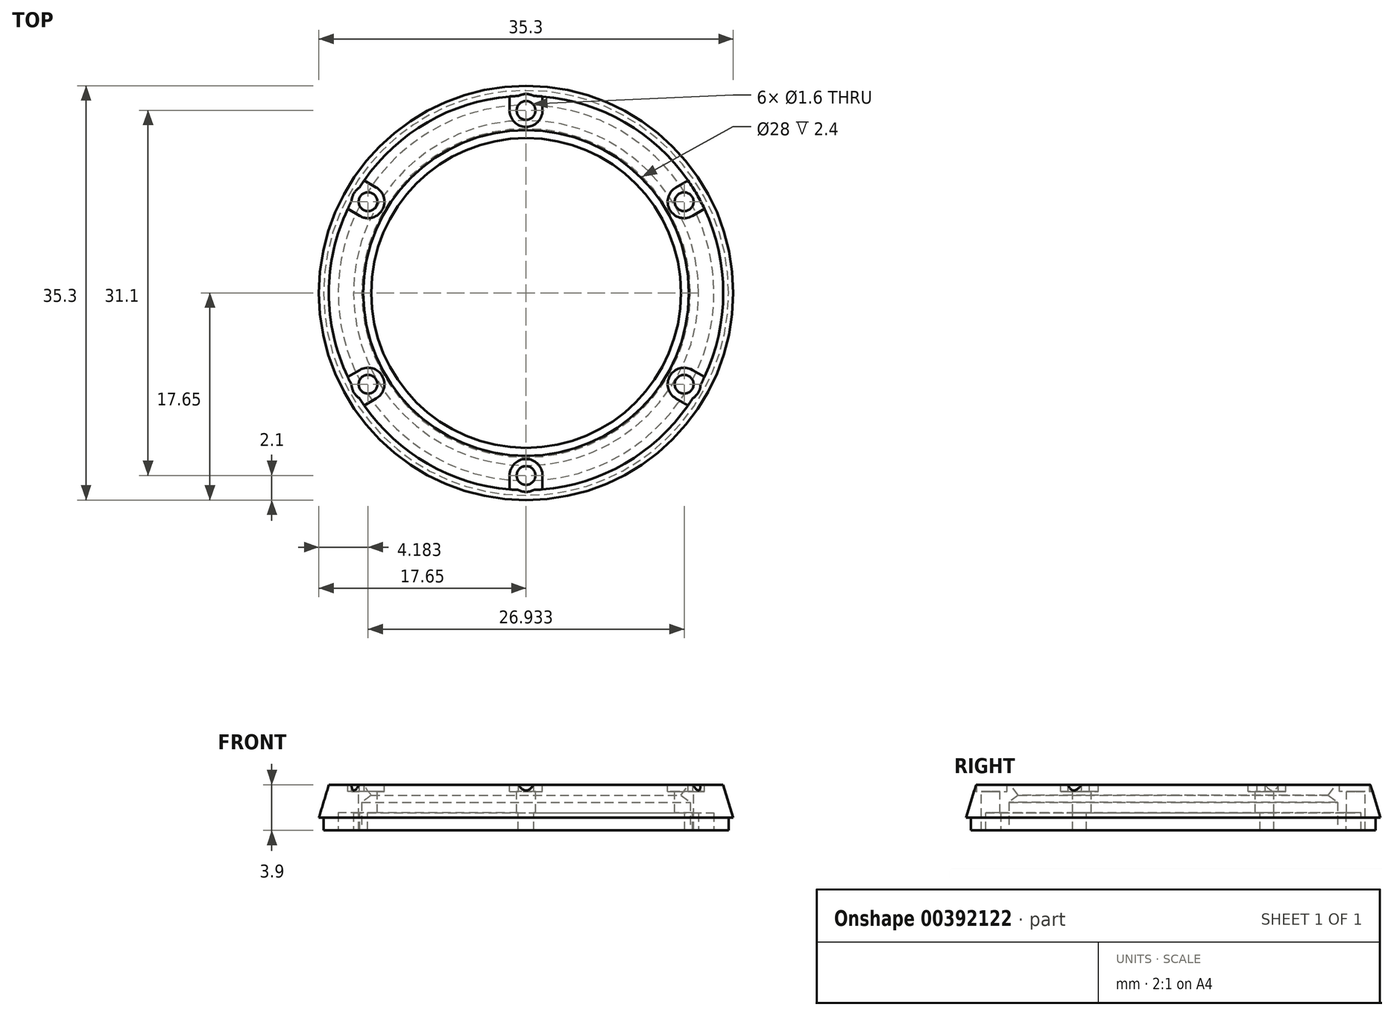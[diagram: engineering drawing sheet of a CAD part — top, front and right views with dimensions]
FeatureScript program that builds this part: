
annotation { "Feature Type Name" : "Feature", "Feature Type Description" : "" }
export const myFeature = defineFeature(function(context is Context, id is Id, definition is map)
    precondition{}
    {
        {
            var Q0;
            Q0=qCreatedBy(makeId("Front.planeOp"),FACE);
            var sketch = newSketch(context, id + "F0", { "sketchPlane" : qUnion([Q0])});
            skLineSegment(sketch, "E0", {"start": v(0, 0) * mm, "end": v(0, 11.47) * mm, "construction": true});
            skLineSegment(sketch, "E1", {"start": v(0, 0) * mm, "end": v(-14, 0) * mm, "construction": true});
            skLineSegment(sketch, "E2", {"start": v(-14, 0) * mm, "end": v(-14, 2.4) * mm});
            skLineSegment(sketch, "E3", {"start": v(-14, 2.4) * mm, "end": v(-13.2, 3) * mm});
            skLineSegment(sketch, "E4", {"start": v(-13.2, 3) * mm, "end": v(-13.88, 3.9) * mm});
            skLineSegment(sketch, "E5", {"start": v(-13.88, 3.9) * mm, "end": v(-16.8, 3.9) * mm});
            skLineSegment(sketch, "E6", {"start": v(-16.8, 3.9) * mm, "end": v(-17.65, 1.1) * mm});
            skLineSegment(sketch, "E7", {"start": v(-17.65, 1.1) * mm, "end": v(-17.25, 1.1) * mm});
            skLineSegment(sketch, "E8", {"start": v(-17.25, 1.1) * mm, "end": v(-17.25, 0) * mm});
            skLineSegment(sketch, "E9", {"start": v(-17.25, 0) * mm, "end": v(-14, 0) * mm});
            skLineSegment(sketch, "E10", {"start": v(-14.7, 0) * mm, "end": v(-14.7, 1.5) * mm});
            skLineSegment(sketch, "E11", {"start": v(-14.7, 1.5) * mm, "end": v(-16, 1.5) * mm});
            skLineSegment(sketch, "E12", {"start": v(-16, 1.5) * mm, "end": v(-16, 0) * mm});
            skSolve(sketch);
        }
        {
            var Q0;
            Q0=makeQuery(id+"F0.imprint","IMPRINT",FACE,{"disambiguationData":[TD([[makeQuery(id+"F0.imprint","IMPRINT",EDGE,{"derivedFrom":sQuery(id+"F0.wireOp",EDGE,"E2")}),1.0]])]});
            var Q1;
            Q1=sQuery(id+"F0.wireOp",EDGE,"E0");
            revolve(context, id + "F1", {"entities" : qUnion([Q0]), "axis" : qUnion([Q1]), "revolveType" : RevolveType.FULL});
        }
        {
            var Q0;
            Q0=makeQuery(id+"F1.opRevolve","SWEPT_FACE",FACE,{"disambiguationData":[OSD([sQuery(id+"F0.wireOp",EDGE,"E5")])]});
            var sketch = newSketch(context, id + "F2", { "sketchPlane" : qUnion([Q0])});
            skCircle(sketch, "E13", {"center": v(0, 15.55) * mm, "radius": 1.4 * mm});
            skLineSegment(sketch, "E14", {"start": v(-1.4, 15.55) * mm, "end": v(-1.4, 17.6) * mm});
            skLineSegment(sketch, "E15", {"start": v(1.4, 15.55) * mm, "end": v(1.4, 17.6) * mm});
            skCircle(sketch, "E16.0", {"center": v(0, 0) * mm, "radius": 17.65 * mm});
            skCircle(sketch, "E17", {"center": v(0, 15.55) * mm, "radius": 0.8 * mm});
            skCircle(sketch, "E18.1.0", {"center": v(-13.47, 7.78) * mm, "radius": 1.4 * mm});
            skLineSegment(sketch, "E18.1.1", {"start": v(-14.17, 6.56) * mm, "end": v(-15.94, 7.58) * mm});
            skCircle(sketch, "E18.1.2", {"center": v(-13.47, 7.78) * mm, "radius": 0.8 * mm});
            skLineSegment(sketch, "E18.1.3", {"start": v(-12.77, 8.99) * mm, "end": v(-14.54, 10) * mm});
            skCircle(sketch, "E18.2.0", {"center": v(-13.47, -7.77) * mm, "radius": 1.4 * mm});
            skLineSegment(sketch, "E18.2.1", {"start": v(-12.77, -8.99) * mm, "end": v(-14.54, -10) * mm});
            skCircle(sketch, "E18.2.2", {"center": v(-13.47, -7.77) * mm, "radius": 0.8 * mm});
            skLineSegment(sketch, "E18.2.3", {"start": v(-14.17, -6.56) * mm, "end": v(-15.94, -7.58) * mm});
            skCircle(sketch, "E18.3.0", {"center": v(0, -15.55) * mm, "radius": 1.4 * mm});
            skLineSegment(sketch, "E18.3.1", {"start": v(1.4, -15.55) * mm, "end": v(1.4, -17.6) * mm});
            skCircle(sketch, "E18.3.2", {"center": v(0, -15.55) * mm, "radius": 0.8 * mm});
            skLineSegment(sketch, "E18.3.3", {"start": v(-1.4, -15.55) * mm, "end": v(-1.4, -17.6) * mm});
            skCircle(sketch, "E18.4.0", {"center": v(13.47, -7.78) * mm, "radius": 1.4 * mm});
            skLineSegment(sketch, "E18.4.1", {"start": v(14.17, -6.56) * mm, "end": v(15.94, -7.58) * mm});
            skCircle(sketch, "E18.4.2", {"center": v(13.47, -7.78) * mm, "radius": 0.8 * mm});
            skLineSegment(sketch, "E18.4.3", {"start": v(12.77, -8.99) * mm, "end": v(14.54, -10) * mm});
            skCircle(sketch, "E18.5.0", {"center": v(13.47, 7.78) * mm, "radius": 1.4 * mm});
            skLineSegment(sketch, "E18.5.1", {"start": v(12.77, 8.99) * mm, "end": v(14.54, 10) * mm});
            skCircle(sketch, "E18.5.2", {"center": v(13.47, 7.78) * mm, "radius": 0.8 * mm});
            skLineSegment(sketch, "E18.5.3", {"start": v(14.17, 6.56) * mm, "end": v(15.94, 7.58) * mm});
            skSolve(sketch);
        }
        {
            var Q0;
            Q0=makeQuery(id+"F2.imprint","IMPRINT",FACE,{"disambiguationData":[TD([[makeQuery(id+"F2.imprint","IMPRINT",EDGE,{"derivedFrom":sQuery(id+"F2.wireOp",EDGE,"E17")}),1.0]])]});
            var Q1;
            Q1=makeQuery(id+"F2.imprint","IMPRINT",FACE,{"disambiguationData":[TD([[makeQuery(id+"F2.imprint","IMPRINT",EDGE,{"derivedFrom":sQuery(id+"F2.wireOp",EDGE,"E18.5.2")}),1.0]])]});
            var Q2;
            Q2=makeQuery(id+"F2.imprint","IMPRINT",FACE,{"disambiguationData":[TD([[makeQuery(id+"F2.imprint","IMPRINT",EDGE,{"derivedFrom":sQuery(id+"F2.wireOp",EDGE,"E18.4.2")}),1.0]])]});
            var Q3;
            Q3=makeQuery(id+"F2.imprint","IMPRINT",FACE,{"disambiguationData":[TD([[makeQuery(id+"F2.imprint","IMPRINT",EDGE,{"derivedFrom":sQuery(id+"F2.wireOp",EDGE,"E18.1.2")}),1.0]])]});
            var Q4;
            Q4=makeQuery(id+"F2.imprint","IMPRINT",FACE,{"disambiguationData":[TD([[makeQuery(id+"F2.imprint","IMPRINT",EDGE,{"derivedFrom":sQuery(id+"F2.wireOp",EDGE,"E18.3.2")}),1.0]])]});
            var Q5;
            Q5=makeQuery(id+"F2.imprint","IMPRINT",FACE,{"disambiguationData":[TD([[makeQuery(id+"F2.imprint","IMPRINT",EDGE,{"derivedFrom":sQuery(id+"F2.wireOp",EDGE,"E18.2.2")}),1.0]])]});
            extrude(context, id + "F3", {"entities" : qUnion([Q0, Q1, Q2, Q3, Q4, Q5]), "operationType" : NewBodyOperationType.REMOVE, "endBound" : BoundingType.THROUGH_ALL, "oppositeDirection" : true, "depth" : 25 * mm});
        }
        {
            var Q0;
            Q0=makeQuery(id+"F2.imprint","IMPRINT",FACE,{"disambiguationData":[TD([[makeQuery(id+"F2.imprint","IMPRINT",EDGE,{"derivedFrom":sQuery(id+"F2.wireOp",EDGE,"E17")}),-1.0]])]});
            var Q1;
            {var subQ0=sQuery(id+"F2.wireOp",EDGE,"E15");var subQ1=sQuery(id+"F2.wireOp",EDGE,"E13");var subQ2=makeQuery(id+"F2.imprint","INTERSECT",VERTEX,{"derivedFrom":[subQ1,subQ0]});Q1=makeQuery(id+"F2.imprint","IMPRINT",FACE,{"disambiguationData":[TD([[makeQuery(id+"F2.imprint","IMPRINT",EDGE,{"disambiguationData":[TD([[subQ2,-1.0]])],"derivedFrom":subQ1}),-1.0]])]});}
            var Q2;
            {var subQ0=sQuery(id+"F2.wireOp",EDGE,"E16.0");var subQ5=sQuery(id+"F2.wireOp",EDGE,"E14");var subQ6=makeQuery(id+"F2.imprint","INTERSECT",VERTEX,{"derivedFrom":[subQ5,subQ0]});Q2=makeQuery(id+"F2.imprint","IMPRINT",FACE,{"disambiguationData":[TD([[makeQuery(id+"F2.imprint","IMPRINT",EDGE,{"disambiguationData":[TD([[subQ6,-1.0]])],"derivedFrom":subQ0}),-1.0]])]});}
            var Q3;
            {var subQ0=sQuery(id+"F2.wireOp",EDGE,"E14");var subQ1=sQuery(id+"F2.wireOp",EDGE,"E13");var subQ2=makeQuery(id+"F2.imprint","INTERSECT",VERTEX,{"derivedFrom":[subQ1,subQ0]});Q3=makeQuery(id+"F2.imprint","IMPRINT",FACE,{"disambiguationData":[TD([[makeQuery(id+"F2.imprint","IMPRINT",EDGE,{"disambiguationData":[TD([[subQ2,1.0]])],"derivedFrom":subQ1}),-1.0]])]});}
            var Q4;
            Q4=makeQuery(id+"F2.imprint","IMPRINT",FACE,{"disambiguationData":[TD([[makeQuery(id+"F2.imprint","IMPRINT",EDGE,{"derivedFrom":sQuery(id+"F2.wireOp",EDGE,"E18.5.2")}),-1.0]])]});
            var Q5;
            {var subQ0=sQuery(id+"F2.wireOp",EDGE,"E18.5.1");var subQ1=sQuery(id+"F2.wireOp",EDGE,"E18.5.0");var subQ2=makeQuery(id+"F2.imprint","INTERSECT",VERTEX,{"derivedFrom":[subQ1,subQ0]});Q5=makeQuery(id+"F2.imprint","IMPRINT",FACE,{"disambiguationData":[TD([[makeQuery(id+"F2.imprint","IMPRINT",EDGE,{"disambiguationData":[TD([[subQ2,1.0]])],"derivedFrom":subQ1}),-1.0]])]});}
            var Q6;
            {var subQ0=sQuery(id+"F2.wireOp",EDGE,"E18.5.3");var subQ1=sQuery(id+"F2.wireOp",EDGE,"E18.5.0");var subQ2=makeQuery(id+"F2.imprint","INTERSECT",VERTEX,{"derivedFrom":[subQ1,subQ0]});Q6=makeQuery(id+"F2.imprint","IMPRINT",FACE,{"disambiguationData":[TD([[makeQuery(id+"F2.imprint","IMPRINT",EDGE,{"disambiguationData":[TD([[subQ2,-1.0]])],"derivedFrom":subQ1}),-1.0]])]});}
            var Q7;
            {var subQ1=sQuery(id+"F2.wireOp",EDGE,"E16.0");var subQ5=sQuery(id+"F2.wireOp",EDGE,"E18.5.1");var subQ6=makeQuery(id+"F2.imprint","INTERSECT",VERTEX,{"derivedFrom":[subQ1,subQ5]});Q7=makeQuery(id+"F2.imprint","IMPRINT",FACE,{"disambiguationData":[TD([[makeQuery(id+"F2.imprint","IMPRINT",EDGE,{"disambiguationData":[TD([[subQ6,-1.0]])],"derivedFrom":subQ1}),-1.0]])]});}
            var Q8;
            {var subQ0=sQuery(id+"F2.wireOp",EDGE,"E18.4.1");var subQ1=sQuery(id+"F2.wireOp",EDGE,"E18.4.0");var subQ2=makeQuery(id+"F2.imprint","INTERSECT",VERTEX,{"derivedFrom":[subQ1,subQ0]});Q8=makeQuery(id+"F2.imprint","IMPRINT",FACE,{"disambiguationData":[TD([[makeQuery(id+"F2.imprint","IMPRINT",EDGE,{"disambiguationData":[TD([[subQ2,1.0]])],"derivedFrom":subQ1}),-1.0]])]});}
            var Q9;
            Q9=makeQuery(id+"F2.imprint","IMPRINT",FACE,{"disambiguationData":[TD([[makeQuery(id+"F2.imprint","IMPRINT",EDGE,{"derivedFrom":sQuery(id+"F2.wireOp",EDGE,"E18.4.2")}),-1.0]])]});
            var Q10;
            {var subQ0=sQuery(id+"F2.wireOp",EDGE,"E18.4.3");var subQ1=sQuery(id+"F2.wireOp",EDGE,"E18.4.0");var subQ2=makeQuery(id+"F2.imprint","INTERSECT",VERTEX,{"derivedFrom":[subQ1,subQ0]});Q10=makeQuery(id+"F2.imprint","IMPRINT",FACE,{"disambiguationData":[TD([[makeQuery(id+"F2.imprint","IMPRINT",EDGE,{"disambiguationData":[TD([[subQ2,-1.0]])],"derivedFrom":subQ1}),-1.0]])]});}
            var Q11;
            {var subQ0=sQuery(id+"F2.wireOp",EDGE,"E18.4.0");var subQ1=makeQuery(id+"F1.opRevolve","SWEPT_EDGE",EDGE,{"disambiguationData":[OSD([sQuery(id+"F0.wireOp",EDGE,"E5"),sQuery(id+"F0.wireOp",EDGE,"E6")])]});var subQ2=makeQuery(id+"F2.imprint","INTERSECT",VERTEX,{"disambiguationData":[OD(0.0)],"derivedFrom":[subQ1,subQ0]});Q11=makeQuery(id+"F2.imprint","IMPRINT",FACE,{"disambiguationData":[TD([[makeQuery(id+"F2.imprint","IMPRINT",EDGE,{"disambiguationData":[TD([[subQ2,-1.0]])],"derivedFrom":subQ0}),1.0]])]});}
            var Q12;
            {var subQ1=sQuery(id+"F2.wireOp",EDGE,"E16.0");var subQ8=sQuery(id+"F2.wireOp",EDGE,"E18.4.1");var subQ9=makeQuery(id+"F2.imprint","INTERSECT",VERTEX,{"derivedFrom":[subQ1,subQ8]});Q12=makeQuery(id+"F2.imprint","IMPRINT",FACE,{"disambiguationData":[TD([[makeQuery(id+"F2.imprint","IMPRINT",EDGE,{"disambiguationData":[TD([[subQ9,-1.0]])],"derivedFrom":subQ1}),-1.0]])]});}
            var Q13;
            {var subQ0=sQuery(id+"F2.wireOp",EDGE,"E18.5.0");var subQ1=makeQuery(id+"F1.opRevolve","SWEPT_EDGE",EDGE,{"disambiguationData":[OSD([sQuery(id+"F0.wireOp",EDGE,"E5"),sQuery(id+"F0.wireOp",EDGE,"E6")])]});var subQ2=makeQuery(id+"F2.imprint","INTERSECT",VERTEX,{"disambiguationData":[OD(0.0)],"derivedFrom":[subQ1,subQ0]});Q13=makeQuery(id+"F2.imprint","IMPRINT",FACE,{"disambiguationData":[TD([[makeQuery(id+"F2.imprint","IMPRINT",EDGE,{"disambiguationData":[TD([[subQ2,-1.0]])],"derivedFrom":subQ0}),1.0]])]});}
            var Q14;
            {var subQ0=sQuery(id+"F2.wireOp",EDGE,"E13");var subQ1=makeQuery(id+"F1.opRevolve","SWEPT_EDGE",EDGE,{"disambiguationData":[OSD([sQuery(id+"F0.wireOp",EDGE,"E5"),sQuery(id+"F0.wireOp",EDGE,"E6")])]});var subQ2=makeQuery(id+"F2.imprint","INTERSECT",VERTEX,{"disambiguationData":[OD(0.0)],"derivedFrom":[subQ1,subQ0]});Q14=makeQuery(id+"F2.imprint","IMPRINT",FACE,{"disambiguationData":[TD([[makeQuery(id+"F2.imprint","IMPRINT",EDGE,{"disambiguationData":[TD([[subQ2,-1.0]])],"derivedFrom":subQ0}),1.0]])]});}
            var Q15;
            Q15=makeQuery(id+"F2.imprint","IMPRINT",FACE,{"disambiguationData":[TD([[makeQuery(id+"F2.imprint","IMPRINT",EDGE,{"derivedFrom":sQuery(id+"F2.wireOp",EDGE,"E18.1.2")}),-1.0]])]});
            var Q16;
            {var subQ0=sQuery(id+"F2.wireOp",EDGE,"E18.1.1");var subQ1=sQuery(id+"F2.wireOp",EDGE,"E16.0");var subQ2=makeQuery(id+"F2.imprint","INTERSECT",VERTEX,{"derivedFrom":[subQ1,subQ0]});Q16=makeQuery(id+"F2.imprint","IMPRINT",FACE,{"disambiguationData":[TD([[makeQuery(id+"F2.imprint","IMPRINT",EDGE,{"disambiguationData":[TD([[subQ2,-1.0]])],"derivedFrom":subQ1}),-1.0]])]});}
            var Q17;
            {var subQ0=sQuery(id+"F2.wireOp",EDGE,"E18.1.3");var subQ1=sQuery(id+"F2.wireOp",EDGE,"E18.1.0");var subQ2=makeQuery(id+"F2.imprint","INTERSECT",VERTEX,{"derivedFrom":[subQ1,subQ0]});Q17=makeQuery(id+"F2.imprint","IMPRINT",FACE,{"disambiguationData":[TD([[makeQuery(id+"F2.imprint","IMPRINT",EDGE,{"disambiguationData":[TD([[subQ2,-1.0]])],"derivedFrom":subQ1}),-1.0]])]});}
            var Q18;
            {var subQ0=sQuery(id+"F2.wireOp",EDGE,"E18.1.1");var subQ1=sQuery(id+"F2.wireOp",EDGE,"E18.1.0");var subQ2=makeQuery(id+"F2.imprint","INTERSECT",VERTEX,{"derivedFrom":[subQ1,subQ0]});Q18=makeQuery(id+"F2.imprint","IMPRINT",FACE,{"disambiguationData":[TD([[makeQuery(id+"F2.imprint","IMPRINT",EDGE,{"disambiguationData":[TD([[subQ2,1.0]])],"derivedFrom":subQ1}),-1.0]])]});}
            var Q19;
            Q19=makeQuery(id+"F2.imprint","IMPRINT",FACE,{"disambiguationData":[TD([[makeQuery(id+"F2.imprint","IMPRINT",EDGE,{"derivedFrom":sQuery(id+"F2.wireOp",EDGE,"E18.2.2")}),-1.0]])]});
            var Q20;
            {var subQ0=sQuery(id+"F2.wireOp",EDGE,"E18.2.3");var subQ1=sQuery(id+"F2.wireOp",EDGE,"E18.2.0");var subQ2=makeQuery(id+"F2.imprint","INTERSECT",VERTEX,{"derivedFrom":[subQ1,subQ0]});Q20=makeQuery(id+"F2.imprint","IMPRINT",FACE,{"disambiguationData":[TD([[makeQuery(id+"F2.imprint","IMPRINT",EDGE,{"disambiguationData":[TD([[subQ2,-1.0]])],"derivedFrom":subQ1}),-1.0]])]});}
            var Q21;
            {var subQ1=sQuery(id+"F2.wireOp",EDGE,"E16.0");var subQ5=sQuery(id+"F2.wireOp",EDGE,"E18.2.1");var subQ6=makeQuery(id+"F2.imprint","INTERSECT",VERTEX,{"derivedFrom":[subQ1,subQ5]});Q21=makeQuery(id+"F2.imprint","IMPRINT",FACE,{"disambiguationData":[TD([[makeQuery(id+"F2.imprint","IMPRINT",EDGE,{"disambiguationData":[TD([[subQ6,-1.0]])],"derivedFrom":subQ1}),-1.0]])]});}
            var Q22;
            {var subQ0=sQuery(id+"F2.wireOp",EDGE,"E18.2.0");var subQ1=makeQuery(id+"F1.opRevolve","SWEPT_EDGE",EDGE,{"disambiguationData":[OSD([sQuery(id+"F0.wireOp",EDGE,"E5"),sQuery(id+"F0.wireOp",EDGE,"E6")])]});var subQ2=makeQuery(id+"F2.imprint","INTERSECT",VERTEX,{"disambiguationData":[OD(0.0)],"derivedFrom":[subQ1,subQ0]});Q22=makeQuery(id+"F2.imprint","IMPRINT",FACE,{"disambiguationData":[TD([[makeQuery(id+"F2.imprint","IMPRINT",EDGE,{"disambiguationData":[TD([[subQ2,-1.0]])],"derivedFrom":subQ0}),1.0]])]});}
            var Q23;
            {var subQ0=sQuery(id+"F2.wireOp",EDGE,"E18.2.1");var subQ1=sQuery(id+"F2.wireOp",EDGE,"E18.2.0");var subQ2=makeQuery(id+"F2.imprint","INTERSECT",VERTEX,{"derivedFrom":[subQ1,subQ0]});Q23=makeQuery(id+"F2.imprint","IMPRINT",FACE,{"disambiguationData":[TD([[makeQuery(id+"F2.imprint","IMPRINT",EDGE,{"disambiguationData":[TD([[subQ2,1.0]])],"derivedFrom":subQ1}),-1.0]])]});}
            var Q24;
            {var subQ0=sQuery(id+"F2.wireOp",EDGE,"E18.3.3");var subQ1=sQuery(id+"F2.wireOp",EDGE,"E18.3.0");var subQ2=makeQuery(id+"F2.imprint","INTERSECT",VERTEX,{"derivedFrom":[subQ1,subQ0]});Q24=makeQuery(id+"F2.imprint","IMPRINT",FACE,{"disambiguationData":[TD([[makeQuery(id+"F2.imprint","IMPRINT",EDGE,{"disambiguationData":[TD([[subQ2,-1.0]])],"derivedFrom":subQ1}),-1.0]])]});}
            var Q25;
            {var subQ0=sQuery(id+"F2.wireOp",EDGE,"E18.3.1");var subQ1=sQuery(id+"F2.wireOp",EDGE,"E18.3.0");var subQ2=makeQuery(id+"F2.imprint","INTERSECT",VERTEX,{"derivedFrom":[subQ1,subQ0]});Q25=makeQuery(id+"F2.imprint","IMPRINT",FACE,{"disambiguationData":[TD([[makeQuery(id+"F2.imprint","IMPRINT",EDGE,{"disambiguationData":[TD([[subQ2,1.0]])],"derivedFrom":subQ1}),-1.0]])]});}
            var Q26;
            {var subQ1=sQuery(id+"F2.wireOp",EDGE,"E16.0");var subQ5=sQuery(id+"F2.wireOp",EDGE,"E18.3.1");var subQ6=makeQuery(id+"F2.imprint","INTERSECT",VERTEX,{"derivedFrom":[subQ1,subQ5]});Q26=makeQuery(id+"F2.imprint","IMPRINT",FACE,{"disambiguationData":[TD([[makeQuery(id+"F2.imprint","IMPRINT",EDGE,{"disambiguationData":[TD([[subQ6,-1.0]])],"derivedFrom":subQ1}),-1.0]])]});}
            var Q27;
            {var subQ0=sQuery(id+"F2.wireOp",EDGE,"E18.3.0");var subQ1=makeQuery(id+"F1.opRevolve","SWEPT_EDGE",EDGE,{"disambiguationData":[OSD([sQuery(id+"F0.wireOp",EDGE,"E5"),sQuery(id+"F0.wireOp",EDGE,"E6")])]});var subQ2=makeQuery(id+"F2.imprint","INTERSECT",VERTEX,{"disambiguationData":[OD(0.0)],"derivedFrom":[subQ1,subQ0]});Q27=makeQuery(id+"F2.imprint","IMPRINT",FACE,{"disambiguationData":[TD([[makeQuery(id+"F2.imprint","IMPRINT",EDGE,{"disambiguationData":[TD([[subQ2,-1.0]])],"derivedFrom":subQ0}),1.0]])]});}
            var Q28;
            Q28=makeQuery(id+"F2.imprint","IMPRINT",FACE,{"disambiguationData":[TD([[makeQuery(id+"F2.imprint","IMPRINT",EDGE,{"derivedFrom":sQuery(id+"F2.wireOp",EDGE,"E18.3.2")}),-1.0]])]});
            var Q29;
            {var subQ0=sQuery(id+"F2.wireOp",EDGE,"E18.1.0");var subQ1=makeQuery(id+"F1.opRevolve","SWEPT_EDGE",EDGE,{"disambiguationData":[OSD([sQuery(id+"F0.wireOp",EDGE,"E5"),sQuery(id+"F0.wireOp",EDGE,"E6")])]});var subQ2=makeQuery(id+"F2.imprint","INTERSECT",VERTEX,{"disambiguationData":[OD(0.0)],"derivedFrom":[subQ1,subQ0]});Q29=makeQuery(id+"F2.imprint","IMPRINT",FACE,{"disambiguationData":[TD([[makeQuery(id+"F2.imprint","IMPRINT",EDGE,{"disambiguationData":[TD([[subQ2,-1.0]])],"derivedFrom":subQ0}),1.0]])]});}
            extrude(context, id + "F4", {"entities" : qUnion([Q0, Q1, Q2, Q3, Q4, Q5, Q6, Q7, Q8, Q9, Q10, Q11, Q12, Q13, Q14, Q15, Q16, Q17, Q18, Q19, Q20, Q21, Q22, Q23, Q24, Q25, Q26, Q27, Q28, Q29]), "operationType" : NewBodyOperationType.REMOVE, "oppositeDirection" : true, "depth" : 0.6 * mm});
        }
        {
            var Q0;
            Q0=makeQuery(id+"F3.boolean.opBoolean","SPLIT",FACE,{"disambiguationData":[TD([makeQuery(id+"F1.opRevolve","SWEPT_FACE",FACE,{"disambiguationData":[OSD([sQuery(id+"F0.wireOp",EDGE,"E10")])]}),makeQuery(id+"F1.opRevolve","SWEPT_FACE",FACE,{"disambiguationData":[OSD([sQuery(id+"F0.wireOp",EDGE,"E12")])]}),makeQuery(id+"F3.opExtrude","SWEPT_FACE",FACE,{"disambiguationData":[OSD([sQuery(id+"F2.wireOp",EDGE,"E17")])]}),makeQuery(id+"F3.opExtrude","SWEPT_FACE",FACE,{"disambiguationData":[OSD([sQuery(id+"F2.wireOp",EDGE,"E18.5.2")])]})])],"derivedFrom":makeQuery(id+"F1.opRevolve","SWEPT_FACE",FACE,{"disambiguationData":[OSD([sQuery(id+"F0.wireOp",EDGE,"E11")])]})});
            var sketch = newSketch(context, id + "F5", { "sketchPlane" : qUnion([Q0])});
            skCircle(sketch, "E19", {"center": v(0, -15.55) * mm, "radius": 1.6 * mm});
            skCircle(sketch, "E20.1.0", {"center": v(13.47, -7.78) * mm, "radius": 1.6 * mm});
            skCircle(sketch, "E20.2.0", {"center": v(13.47, 7.77) * mm, "radius": 1.6 * mm});
            skCircle(sketch, "E20.3.0", {"center": v(0, 15.55) * mm, "radius": 1.6 * mm});
            skCircle(sketch, "E20.4.0", {"center": v(-13.47, 7.78) * mm, "radius": 1.6 * mm});
            skCircle(sketch, "E20.5.0", {"center": v(-13.47, -7.78) * mm, "radius": 1.6 * mm});
            skPoint(sketch, "E20.center", {"position": v(0, 0) * mm});
            skCircle(sketch, "E21.0", {"center": v(0, 0) * mm, "radius": 14 * mm});
            skCircle(sketch, "E22.0", {"center": v(0, 0) * mm, "radius": 17.25 * mm});
            skCircle(sketch, "E23.0", {"center": v(0, -15.55) * mm, "radius": 0.8 * mm});
            skCircle(sketch, "E23.1", {"center": v(13.47, -7.78) * mm, "radius": 0.8 * mm});
            skCircle(sketch, "E23.2", {"center": v(13.47, 7.78) * mm, "radius": 0.8 * mm});
            skCircle(sketch, "E23.3", {"center": v(0, 15.55) * mm, "radius": 0.8 * mm});
            skCircle(sketch, "E23.4", {"center": v(-13.47, 7.77) * mm, "radius": 0.8 * mm});
            skCircle(sketch, "E23.5", {"center": v(-13.47, -7.78) * mm, "radius": 0.8 * mm});
            skSolve(sketch);
        }
        {
            var Q0;
            {var subQ0=sQuery(id+"F5.wireOp",EDGE,"E23.1");Q0=makeQuery(id+"F5.imprint","IMPRINT",FACE,{"disambiguationData":[TD([[makeQuery(id+"F5.imprint","IMPRINT",EDGE,{"disambiguationData":[OD(1.0)],"derivedFrom":subQ0}),-1.0]])]});}
            var Q1;
            {var subQ0=sQuery(id+"F5.wireOp",EDGE,"E23.2");Q1=makeQuery(id+"F5.imprint","IMPRINT",FACE,{"disambiguationData":[TD([[makeQuery(id+"F5.imprint","IMPRINT",EDGE,{"disambiguationData":[OD(1.0)],"derivedFrom":subQ0}),-1.0]])]});}
            var Q2;
            {var subQ11=sQuery(id+"F5.wireOp",EDGE,"E23.3");Q2=makeQuery(id+"F5.imprint","IMPRINT",FACE,{"disambiguationData":[TD([[makeQuery(id+"F5.imprint","IMPRINT",EDGE,{"disambiguationData":[OD(1.0)],"derivedFrom":subQ11}),-1.0]])]});}
            var Q3;
            {var subQ0=sQuery(id+"F5.wireOp",EDGE,"E23.4");Q3=makeQuery(id+"F5.imprint","IMPRINT",FACE,{"disambiguationData":[TD([[makeQuery(id+"F5.imprint","IMPRINT",EDGE,{"disambiguationData":[OD(0.0)],"derivedFrom":subQ0}),-1.0]])]});}
            var Q4;
            {var subQ0=sQuery(id+"F5.wireOp",EDGE,"E23.5");Q4=makeQuery(id+"F5.imprint","IMPRINT",FACE,{"disambiguationData":[TD([[makeQuery(id+"F5.imprint","IMPRINT",EDGE,{"disambiguationData":[OD(0.0)],"derivedFrom":subQ0}),-1.0]])]});}
            var Q5;
            {var subQ0=sQuery(id+"F5.wireOp",EDGE,"E23.0");Q5=makeQuery(id+"F5.imprint","IMPRINT",FACE,{"disambiguationData":[TD([[makeQuery(id+"F5.imprint","IMPRINT",EDGE,{"disambiguationData":[OD(0.0)],"derivedFrom":subQ0}),-1.0]])]});}
            var Q6;
            {var subQ0=sQuery(id+"F0.wireOp",EDGE,"E9");Q6=makeQuery(id+"F1.opRevolve","SWEPT_FACE",FACE,{"disambiguationData":[OSD([subQ0]),TDD([makeQuery(id+"F0.imprint","IMPRINT",EDGE,{"disambiguationData":[TD([[makeQuery(id+"F0.imprint","INTERSECT",VERTEX,{"derivedFrom":[sQuery(id+"F0.wireOp",EDGE,"E8"),subQ0]}),-1.0]])],"derivedFrom":subQ0})])]});}
            extrude(context, id + "F6", {"entities" : qUnion([Q0, Q1, Q2, Q3, Q4, Q5]), "operationType" : NewBodyOperationType.ADD, "endBound" : BoundingType.UP_TO_SURFACE, "endBoundEntityFace" : qUnion([Q6]), "depth" : 25 * mm});
        }
    });
